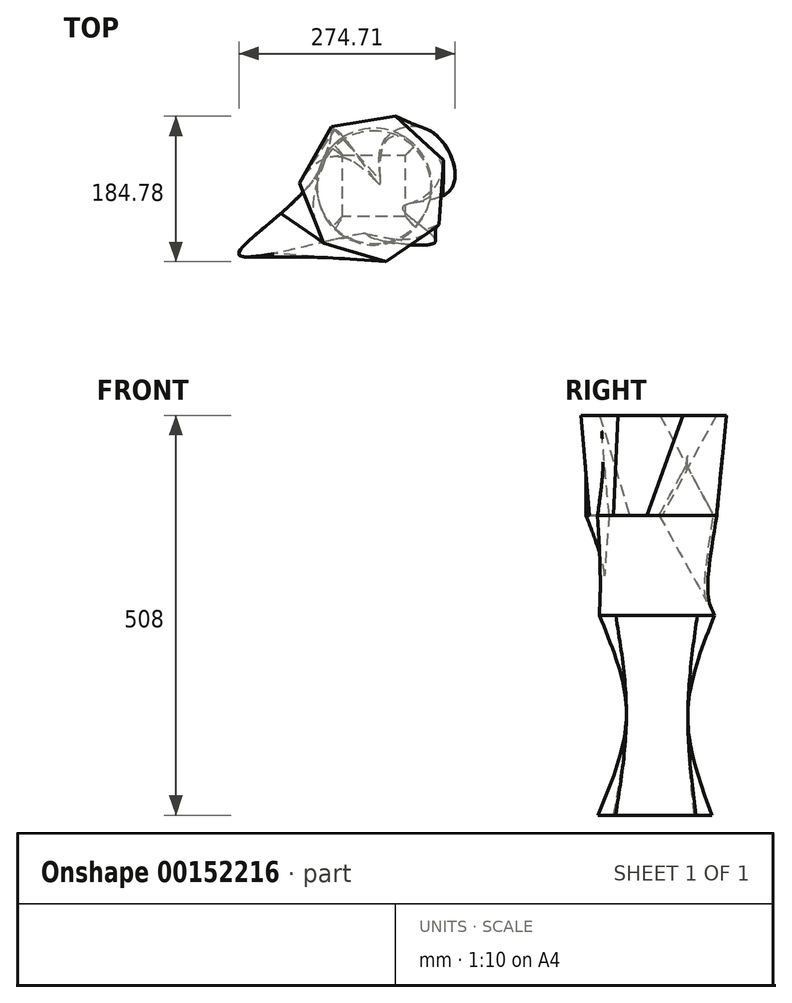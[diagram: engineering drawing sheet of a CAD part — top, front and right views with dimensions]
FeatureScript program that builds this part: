
annotation { "Feature Type Name" : "Feature", "Feature Type Description" : "" }
export const myFeature = defineFeature(function(context is Context, id is Id, definition is map)
    precondition{}
    {
        {
            var Q0;
            Q0=qCreatedBy(makeId("Top.planeOp"),FACE);
            var sketch = newSketch(context, id + "F0", { "sketchPlane" : qUnion([Q0])});
            skCircle(sketch, "E0", {"center": v(0, 0) * mm, "radius": 72.48 * mm});
            skSolve(sketch);
        }
        {
            var Q0;
            Q0=qCreatedBy(makeId("Top.planeOp"),FACE);
            cPlane(context, id + "F1", {"entities" : qUnion([Q0]), "cplaneType" : CPlaneType.OFFSET, "offset" : 127 * mm, "width" : 152.4 * mm, "height" : 152.4 * mm});
        }
        {
            var Q0;
            Q0=qCreatedBy(id+"F1.planeOp",FACE);
            var sketch = newSketch(context, id + "F2", { "sketchPlane" : qUnion([Q0])});
            skLineSegment(sketch, "E1.bottom", {"start": v(39.9, 41.73) * mm, "end": v(-39.9, 41.73) * mm});
            skLineSegment(sketch, "E1.top", {"start": v(39.9, -36.26) * mm, "end": v(-39.9, -36.26) * mm});
            skLineSegment(sketch, "E1.left", {"start": v(39.9, 41.73) * mm, "end": v(39.9, -36.26) * mm});
            skLineSegment(sketch, "E1.right", {"start": v(-39.9, 41.73) * mm, "end": v(-39.9, -36.26) * mm});
            skPoint(sketch, "E1.middle", {"position": v(0, 2.73) * mm});
            skSolve(sketch);
        }
        {
            var Q0;
            Q0=qCreatedBy(id+"F1.planeOp",FACE);
            cPlane(context, id + "F3", {"entities" : qUnion([Q0]), "cplaneType" : CPlaneType.OFFSET, "offset" : 127 * mm, "width" : 152.4 * mm, "height" : 152.4 * mm});
        }
        {
            var Q0;
            Q0=qCreatedBy(id+"F3.planeOp",FACE);
            var sketch = newSketch(context, id + "F4", { "sketchPlane" : qUnion([Q0])});
            skCircle(sketch, "E2", {"center": v(0, 2.6) * mm, "radius": 73.26 * mm});
            skSolve(sketch);
        }
        {
            var Q0;
            Q0=makeQuery(id+"F0.imprint","IMPRINT",FACE,{"disambiguationData":[TD([[makeQuery(id+"F0.imprint","IMPRINT",EDGE,{"derivedFrom":sQuery(id+"F0.wireOp",EDGE,"E0")}),1.0]])]});
            var Q1;
            Q1=makeQuery(id+"F2.imprint","IMPRINT",FACE,{"disambiguationData":[TD([[makeQuery(id+"F2.imprint","IMPRINT",EDGE,{"derivedFrom":sQuery(id+"F2.wireOp",EDGE,"E1.bottom")}),1.0]])]});
            var Q2;
            Q2=makeQuery(id+"F4.imprint","IMPRINT",FACE,{"disambiguationData":[TD([[makeQuery(id+"F4.imprint","IMPRINT",EDGE,{"derivedFrom":sQuery(id+"F4.wireOp",EDGE,"E2")}),1.0]])]});
            loft(context, id + "F5", {"sheetProfilesArray" : [{ "sheetProfileEntities" : qUnion([Q0]) }, { "sheetProfileEntities" : qUnion([Q1]) }, { "sheetProfileEntities" : qUnion([Q2]) }]});
        }
        {
            var Q0;
            Q0=qCreatedBy(id+"F3.planeOp",FACE);
            cPlane(context, id + "F6", {"entities" : qUnion([Q0]), "cplaneType" : CPlaneType.OFFSET, "offset" : 127 * mm, "width" : 152.4 * mm, "height" : 152.4 * mm});
        }
        {
            var Q0;
            Q0=qCreatedBy(id+"F6.planeOp",FACE);
            var sketch = newSketch(context, id + "F7", { "sketchPlane" : qUnion([Q0])});
            skFitSpline(sketch, "E3", {"points": [v(6.54, 5.3) * mm, v(8.79, 52.09) * mm, v(70.64, 72.9) * mm, v(95.02, -4.61) * mm, v(36.08, -25.86) * mm, v(77.98, -68.03) * mm, v(-6.25, -61.92) * mm, v(-11.75, -58.08) * mm, v(-170.24, -86.18) * mm, v(-68.12, 22.93) * mm, v(-48.2, 73.7) * mm, v(6.54, 5.3) * mm]});
            skSolve(sketch);
        }
        {
            var Q0;
            Q0=qCreatedBy(id+"F6.planeOp",FACE);
            cPlane(context, id + "F8", {"entities" : qUnion([Q0]), "cplaneType" : CPlaneType.OFFSET, "offset" : 127 * mm, "width" : 152.4 * mm, "height" : 152.4 * mm});
        }
        {
            var Q0;
            Q0=qCreatedBy(id+"F8.planeOp",FACE);
            var sketch = newSketch(context, id + "F9", { "sketchPlane" : qUnion([Q0])});
            skCircle(sketch, "E4.cCircle", {"center": v(0, 0) * mm, "radius": 85.57 * mm, "construction": true});
            skLineSegment(sketch, "E4.0", {"start": v(27.22, 91) * mm, "end": v(88.11, 35.45) * mm});
            skLineSegment(sketch, "E4.1", {"start": v(88.11, 35.45) * mm, "end": v(82.65, -46.78) * mm});
            skLineSegment(sketch, "E4.2", {"start": v(82.65, -46.78) * mm, "end": v(14.96, -93.8) * mm});
            skLineSegment(sketch, "E4.3", {"start": v(14.96, -93.8) * mm, "end": v(-64, -70.17) * mm});
            skLineSegment(sketch, "E4.4", {"start": v(-64, -70.17) * mm, "end": v(-94.77, 6.29) * mm});
            skLineSegment(sketch, "E4.5", {"start": v(-94.77, 6.29) * mm, "end": v(-54.17, 78.01) * mm});
            skLineSegment(sketch, "E4.6", {"start": v(-54.17, 78.01) * mm, "end": v(27.22, 91) * mm});
            skPoint(sketch, "E4.0.midPoint", {"position": v(57.67, 63.22) * mm});
            skSolve(sketch);
        }
        {
            var Q1;
            Q1=makeQuery(id+"F5.opLoft","CAP_FACE",FACE,{"disambiguationData":[OSD([makeQuery(id+"F4.imprint","IMPRINT",FACE,{"disambiguationData":[TD([[makeQuery(id+"F4.imprint","IMPRINT",EDGE,{"derivedFrom":sQuery(id+"F4.wireOp",EDGE,"E2")}),1.0]])]})])],"isStart":true});
            var Q2;
            Q2=makeQuery(id+"F7.imprint","IMPRINT",FACE,{"disambiguationData":[TD([[makeQuery(id+"F7.imprint","IMPRINT",EDGE,{"derivedFrom":sQuery(id+"F7.wireOp",EDGE,"E3")}),-1.0]])]});
            loft(context, id + "F10", {"operationType" : NewBodyOperationType.ADD, "sheetProfilesArray" : [{ "sheetProfileEntities" : qUnion([Q1]) }, { "sheetProfileEntities" : qUnion([Q2]) }]});
        }
        {
            var Q0;
            Q0=makeQuery(id+"F9.imprint","IMPRINT",FACE,{"disambiguationData":[TD([[makeQuery(id+"F9.imprint","IMPRINT",EDGE,{"derivedFrom":sQuery(id+"F9.wireOp",EDGE,"E4.0")}),-1.0]])]});
            var Q1;
            Q1=makeQuery(id+"F10.opLoft","CAP_FACE",FACE,{"disambiguationData":[OSD([makeQuery(id+"F7.imprint","IMPRINT",FACE,{"disambiguationData":[TD([[makeQuery(id+"F7.imprint","IMPRINT",EDGE,{"derivedFrom":sQuery(id+"F7.wireOp",EDGE,"E3")}),-1.0]])]})])],"isStart":true});
            loft(context, id + "F11", {"sheetProfilesArray" : [{ "sheetProfileEntities" : qUnion([Q0]) }, { "sheetProfileEntities" : qUnion([Q1]) }]});
        }
    });
